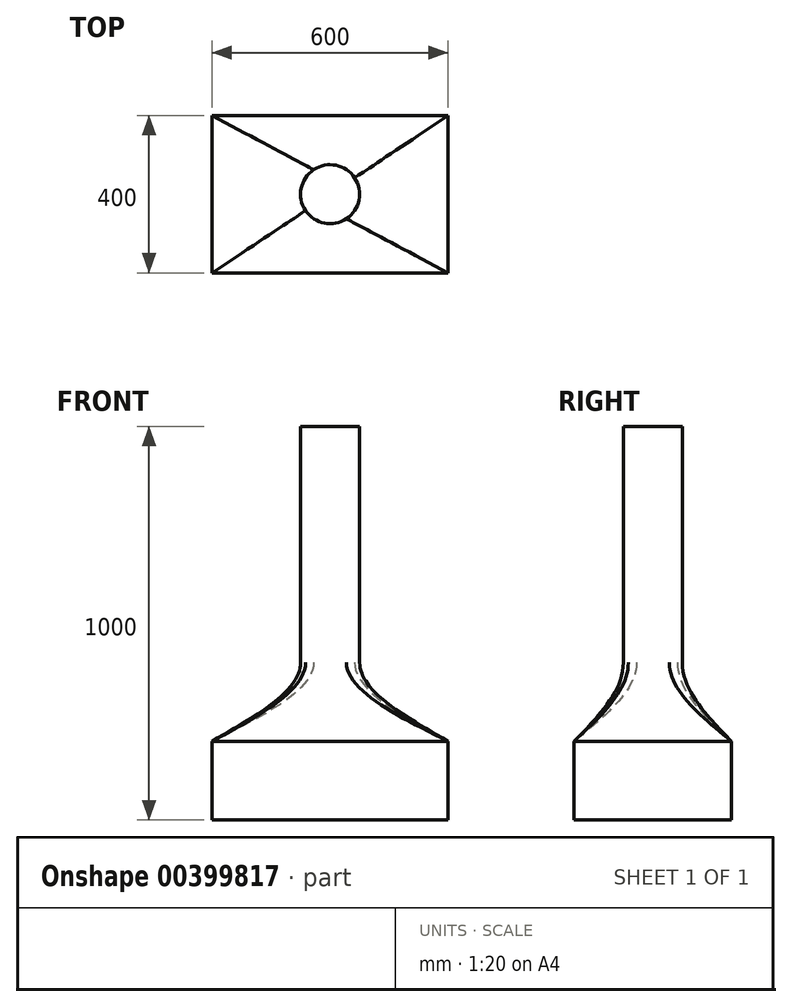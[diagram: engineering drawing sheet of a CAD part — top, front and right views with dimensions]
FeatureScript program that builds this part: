
annotation { "Feature Type Name" : "Feature", "Feature Type Description" : "" }
export const myFeature = defineFeature(function(context is Context, id is Id, definition is map)
    precondition{}
    {
        {
            var Q0;
            Q0=qCreatedBy(makeId("Top.planeOp"),FACE);
            var sketch = newSketch(context, id + "F0", { "sketchPlane" : qUnion([Q0])});
            skLineSegment(sketch, "E0.bottom", {"start": v(300, 200) * mm, "end": v(-300, 200) * mm});
            skLineSegment(sketch, "E0.top", {"start": v(300, -200) * mm, "end": v(-300, -200) * mm});
            skLineSegment(sketch, "E0.left", {"start": v(300, 200) * mm, "end": v(300, -200) * mm});
            skLineSegment(sketch, "E0.right", {"start": v(-300, 200) * mm, "end": v(-300, -200) * mm});
            skPoint(sketch, "E0.middle", {"position": v(0, 0) * mm});
            skSolve(sketch);
        }
        {
            var Q0;
            Q0 = qSketchRegion(id + "F0", true);
            extrude(context, id + "F1", {"entities" : qUnion([Q0]), "depth" : 200 * mm});
        }
        {
            var Q0;
            Q0=qCreatedBy(makeId("Top.planeOp"),FACE);
            cPlane(context, id + "F2", {"entities" : qUnion([Q0]), "cplaneType" : CPlaneType.OFFSET, "offset" : 400 * mm, "width" : 150 * mm, "height" : 150 * mm});
        }
        {
            var Q0;
            Q0=qCreatedBy(id+"F2.planeOp",FACE);
            var sketch = newSketch(context, id + "F3", { "sketchPlane" : qUnion([Q0])});
            skCircle(sketch, "E1", {"center": v(0, 0) * mm, "radius": 75 * mm});
            skSolve(sketch);
        }
        {
            var Q0;
            Q0=makeQuery(id+"F1.opExtrude","CAP_FACE",FACE,{"disambiguationData":[OSD([sQuery(id+"F0.wireOp",EDGE,"E0.bottom"),sQuery(id+"F0.wireOp",EDGE,"E0.top"),sQuery(id+"F0.wireOp",EDGE,"E0.left"),sQuery(id+"F0.wireOp",EDGE,"E0.right")])],"isStart":false});
            var sketch = newSketch(context, id + "F4", { "sketchPlane" : qUnion([Q0])});
            skLineSegment(sketch, "E2.bottom", {"start": v(-300, -200) * mm, "end": v(300, -200) * mm});
            skLineSegment(sketch, "E2.top", {"start": v(-300, 200) * mm, "end": v(300, 200) * mm});
            skLineSegment(sketch, "E2.left", {"start": v(-300, -200) * mm, "end": v(-300, 200) * mm});
            skLineSegment(sketch, "E2.right", {"start": v(300, -200) * mm, "end": v(300, 200) * mm});
            skSolve(sketch);
        }
        {
            var Q1;
            Q1 = qSketchRegion(id + "F3", true);
            var Q2;
            Q2 = qSketchRegion(id + "F4", true);
            loft(context, id + "F5", {"operationType" : NewBodyOperationType.ADD, "startCondition" : LoftEndDerivativeType.NORMAL_TO_PROFILE, "startMagnitude" : 1, "sheetProfilesArray" : [{ "sheetProfileEntities" : qUnion([Q1]) }, { "sheetProfileEntities" : qUnion([Q2]) }]});
        }
        {
            var Q0;
            Q0=makeQuery(id+"F5.opLoft","CAP_FACE",FACE,{"disambiguationData":[OSD([makeQuery(id+"F3.imprint","IMPRINT",FACE,{"disambiguationData":[TD([[makeQuery(id+"F3.imprint","IMPRINT",EDGE,{"derivedFrom":sQuery(id+"F3.wireOp",EDGE,"E1")}),1.0]])]})])],"isStart":true});
            var sketch = newSketch(context, id + "F6", { "sketchPlane" : qUnion([Q0])});
            skCircle(sketch, "E3", {"center": v(0, 0) * mm, "radius": 75 * mm});
            skSolve(sketch);
        }
        {
            var Q0;
            Q0 = qSketchRegion(id + "F6", true);
            extrude(context, id + "F7", {"entities" : qUnion([Q0]), "operationType" : NewBodyOperationType.ADD, "depth" : 600 * mm});
        }
    });
